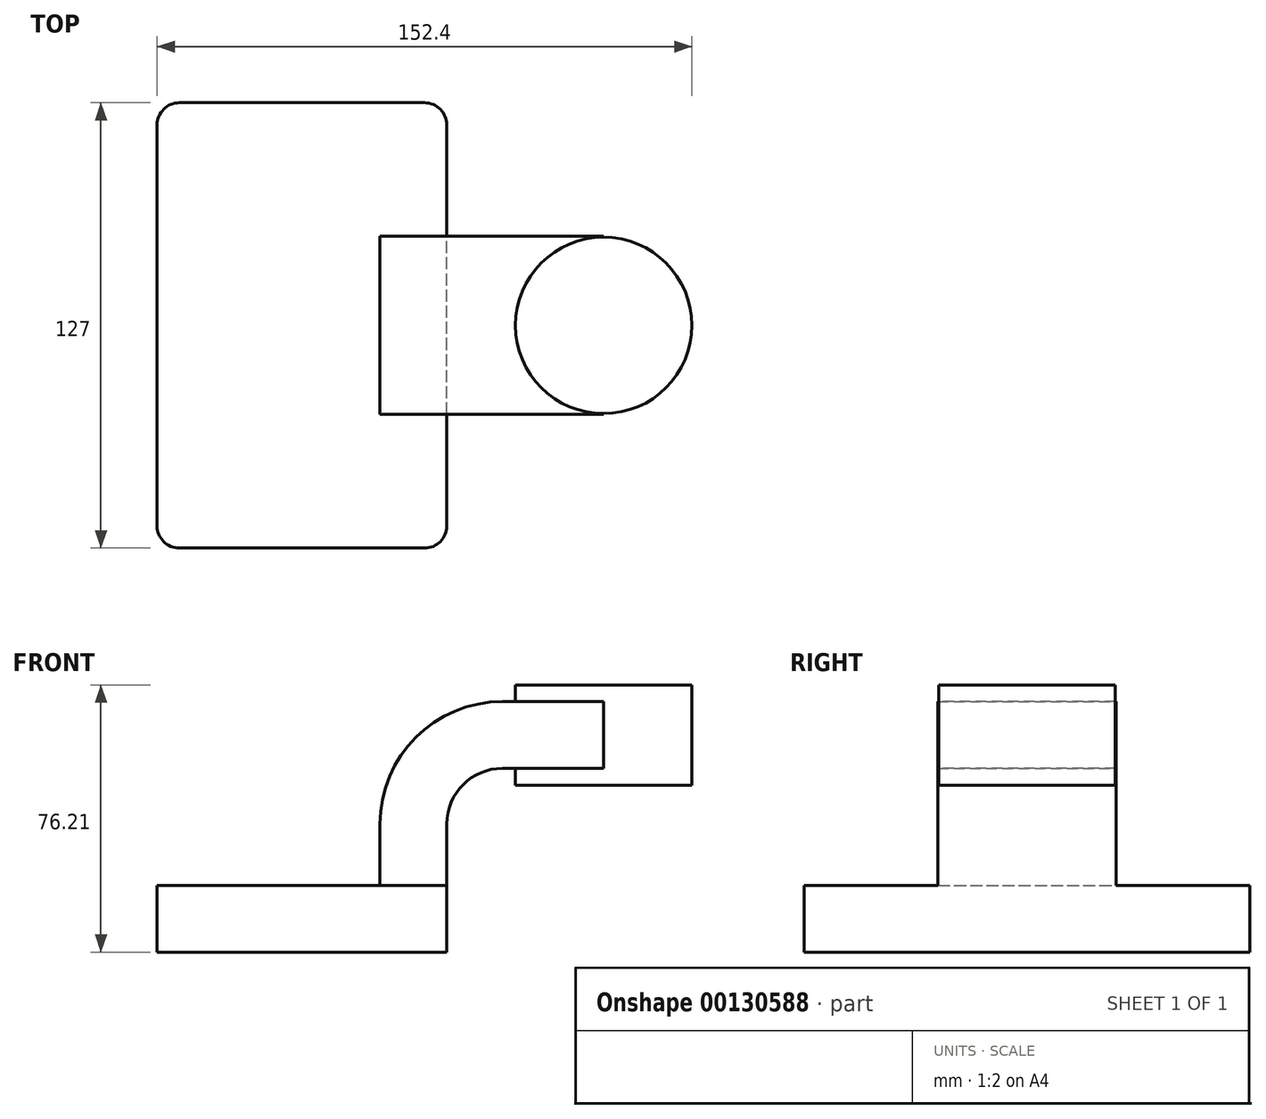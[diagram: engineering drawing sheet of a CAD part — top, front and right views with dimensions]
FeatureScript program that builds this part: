
annotation { "Feature Type Name" : "Feature", "Feature Type Description" : "" }
export const myFeature = defineFeature(function(context is Context, id is Id, definition is map)
    precondition{}
    {
        {
            var Q0;
            Q0=qCreatedBy(makeId("Front.planeOp"),FACE);
            var sketch = newSketch(context, id + "F0", { "sketchPlane" : qUnion([Q0])});
            skLineSegment(sketch, "E0.bottom", {"start": v(41.28, -9.52) * mm, "end": v(-41.28, -9.53) * mm});
            skLineSegment(sketch, "E0.top", {"start": v(41.28, 9.53) * mm, "end": v(-41.28, 9.53) * mm});
            skLineSegment(sketch, "E0.left", {"start": v(41.28, -9.52) * mm, "end": v(41.28, 9.53) * mm});
            skLineSegment(sketch, "E0.right", {"start": v(-41.28, -9.53) * mm, "end": v(-41.28, 9.53) * mm});
            skPoint(sketch, "E0.middle", {"position": v(0, 0) * mm});
            skLineSegment(sketch, "E1.bottom", {"start": v(60.32, 38.1) * mm, "end": v(111.12, 38.1) * mm});
            skLineSegment(sketch, "E1.top", {"start": v(60.32, 66.68) * mm, "end": v(111.12, 66.68) * mm});
            skLineSegment(sketch, "E1.left", {"start": v(60.32, 38.1) * mm, "end": v(60.32, 66.68) * mm});
            skLineSegment(sketch, "E1.right", {"start": v(111.12, 38.1) * mm, "end": v(111.12, 66.68) * mm});
            skPoint(sketch, "E1.middle", {"position": v(85.72, 52.39) * mm});
            skLineSegment(sketch, "E2", {"start": v(41.28, 9.53) * mm, "end": v(41.28, 27) * mm});
            skArc(sketch, "E3", {"start": v(41.27, 27) * mm, "mid": v(45.92, 38.23) * mm, "end": v(57.15, 42.88) * mm});
            skLineSegment(sketch, "E4", {"start": v(57.15, 42.88) * mm, "end": v(85.98, 42.88) * mm});
            skLineSegment(sketch, "E5.0", {"start": v(57.15, 61.93) * mm, "end": v(85.98, 61.93) * mm});
            skArc(sketch, "E5.1", {"start": v(22.23, 27) * mm, "mid": v(32.45, 51.7) * mm, "end": v(57.15, 61.93) * mm});
            skLineSegment(sketch, "E5.2", {"start": v(22.22, 9.53) * mm, "end": v(22.22, 27) * mm});
            skLineSegment(sketch, "E6", {"start": v(85.98, 66.68) * mm, "end": v(85.98, 38.1) * mm});
            skFitSpline(sketch, "E7", {"points": [v(-41.28, 9.52) * mm, v(57.15, 61.93) * mm], "startDerivative": vector(65.73, 102.72) * mm, "endDerivative": vector(123.81, -5.94) * mm});
            skSolve(sketch);
        }
        {
            var Q0;
            Q0=makeQuery(id+"F0.imprint","IMPRINT",FACE,{"disambiguationData":[TD([[makeQuery(id+"F0.imprint","IMPRINT",EDGE,{"derivedFrom":sQuery(id+"F0.wireOp",EDGE,"E0.bottom")}),-1.0]])]});
            extrude(context, id + "F1", {"entities" : qUnion([Q0]), "endBound" : BoundingType.SYMMETRIC, "depth" : 127 * mm});
        }
        {
            var Q0;
            Q0=makeQuery(id+"F0.imprint","IMPRINT",FACE,{"disambiguationData":[TD([[makeQuery(id+"F0.imprint","IMPRINT",EDGE,{"derivedFrom":sQuery(id+"F0.wireOp",EDGE,"E5.1")}),1.0]])]});
            extrude(context, id + "F2", {"entities" : qUnion([Q0]), "operationType" : NewBodyOperationType.ADD, "endBound" : BoundingType.SYMMETRIC, "depth" : 15.88 * mm});
        }
        {
            var Q0;
            {var subQ1=sQuery(id+"F0.wireOp",EDGE,"E2");Q0=makeQuery(id+"F0.imprint","IMPRINT",FACE,{"disambiguationData":[TD([[makeQuery(id+"F0.imprint","IMPRINT",EDGE,{"derivedFrom":subQ1}),1.0]])]});}
            var Q1;
            {var subQ0=sQuery(id+"F0.wireOp",EDGE,"E4");var subQ1=sQuery(id+"F0.wireOp",EDGE,"E1.left");var subQ2=makeQuery(id+"F0.imprint","INTERSECT",VERTEX,{"derivedFrom":[subQ1,subQ0]});Q1=makeQuery(id+"F0.imprint","IMPRINT",FACE,{"disambiguationData":[TD([[makeQuery(id+"F0.imprint","IMPRINT",EDGE,{"disambiguationData":[TD([[subQ2,-1.0]])],"derivedFrom":subQ1}),-1.0]])]});}
            extrude(context, id + "F3", {"entities" : qUnion([Q0, Q1]), "operationType" : NewBodyOperationType.ADD, "endBound" : BoundingType.SYMMETRIC, "depth" : 50.8 * mm});
        }
        {
            var Q0;
            {var subQ0=sQuery(id+"F0.wireOp",EDGE,"E1.right");Q0=makeQuery(id+"F0.imprint","IMPRINT",FACE,{"disambiguationData":[TD([[makeQuery(id+"F0.imprint","IMPRINT",EDGE,{"derivedFrom":subQ0}),1.0]])]});}
            var Q1;
            Q1=sQuery(id+"F0.wireOp",EDGE,"E6");
            revolve(context, id + "F4", {"operationType" : NewBodyOperationType.ADD, "entities" : qUnion([Q0]), "axis" : qUnion([Q1]), "revolveType" : RevolveType.FULL});
        }
        {
            var Q0;
            Q0=makeQuery(id+"F1.opExtrude","CAP_EDGE",EDGE,{"disambiguationData":[OSD([sQuery(id+"F0.wireOp",EDGE,"E0.left")])],"isStart":false});
            var Q1;
            Q1=makeQuery(id+"F1.opExtrude","CAP_EDGE",EDGE,{"disambiguationData":[OSD([sQuery(id+"F0.wireOp",EDGE,"E0.right")])],"isStart":false});
            var Q2;
            Q2=makeQuery(id+"F1.opExtrude","CAP_EDGE",EDGE,{"disambiguationData":[OSD([sQuery(id+"F0.wireOp",EDGE,"E0.left")])],"isStart":true});
            var Q3;
            Q3=makeQuery(id+"F1.opExtrude","CAP_EDGE",EDGE,{"disambiguationData":[OSD([sQuery(id+"F0.wireOp",EDGE,"E0.right")])],"isStart":true});
            fillet(context, id + "F5", {"entities" : qUnion([Q0, Q1, Q2, Q3]), "radius" : 6.35 * mm, "tangentPropagation" : true, "allowEdgeOverflow" : false});
        }
    });
